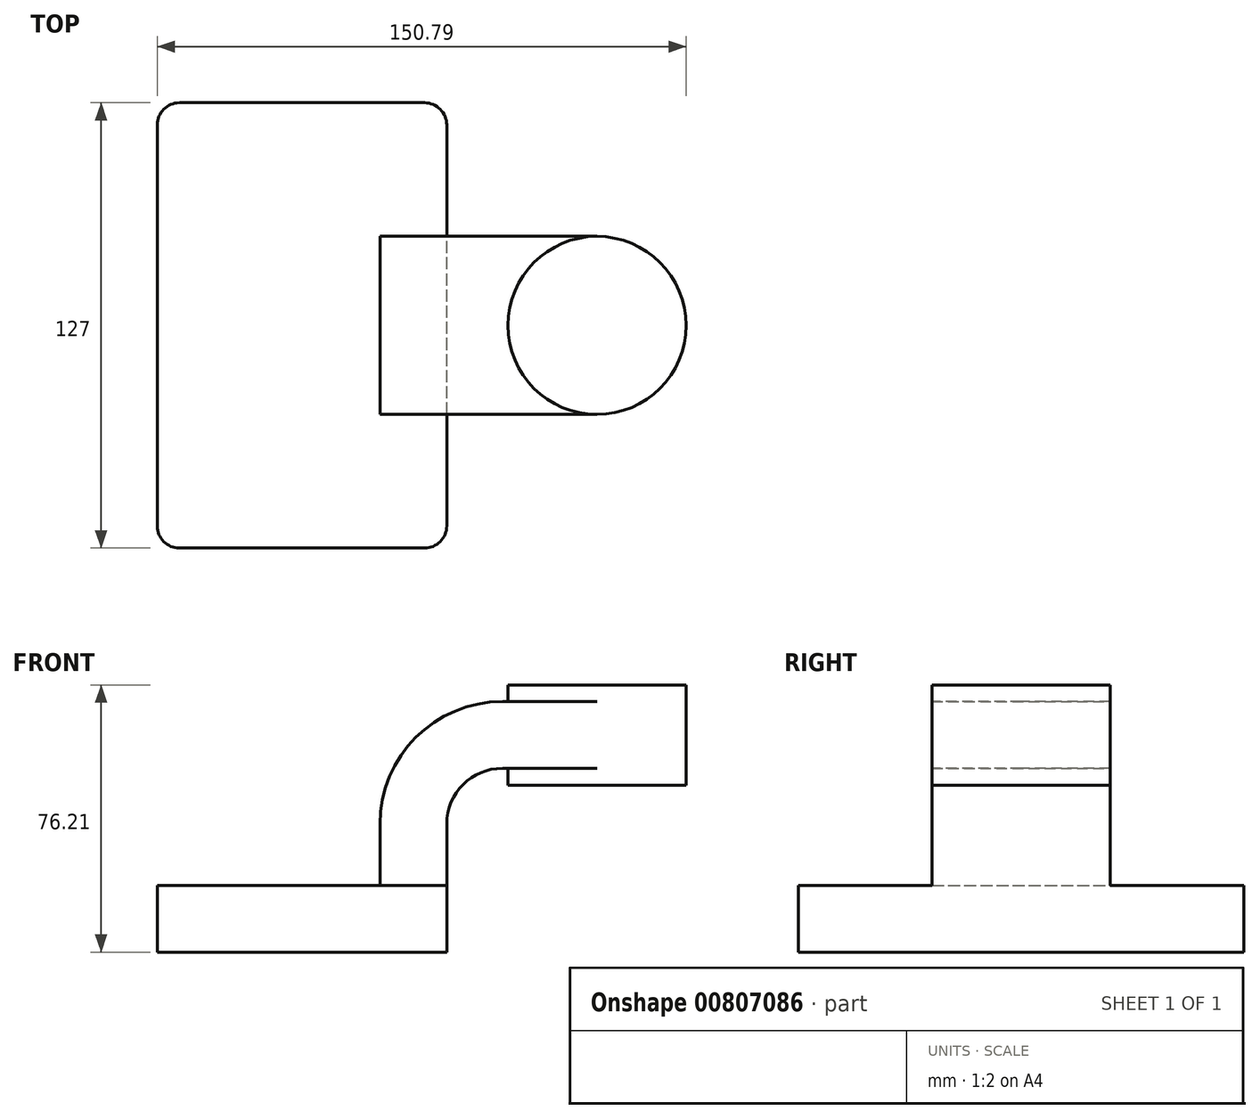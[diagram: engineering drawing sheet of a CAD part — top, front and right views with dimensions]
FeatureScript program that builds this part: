
annotation { "Feature Type Name" : "Feature", "Feature Type Description" : "" }
export const myFeature = defineFeature(function(context is Context, id is Id, definition is map)
    precondition{}
    {
        {
            var Q0;
            Q0=qCreatedBy(makeId("Front.planeOp"),FACE);
            var sketch = newSketch(context, id + "F0", { "sketchPlane" : qUnion([Q0])});
            skLineSegment(sketch, "E0.bottom", {"start": v(41.28, -9.52) * mm, "end": v(-41.27, -9.53) * mm});
            skLineSegment(sketch, "E0.top", {"start": v(41.27, 9.53) * mm, "end": v(-41.28, 9.53) * mm});
            skLineSegment(sketch, "E0.left", {"start": v(41.28, -9.52) * mm, "end": v(41.28, 9.53) * mm});
            skLineSegment(sketch, "E0.right", {"start": v(-41.27, -9.53) * mm, "end": v(-41.28, 9.53) * mm});
            skPoint(sketch, "E0.middle", {"position": v(0, 0) * mm});
            skLineSegment(sketch, "E1.bottom", {"start": v(109.52, 38.1) * mm, "end": v(58.72, 38.1) * mm});
            skLineSegment(sketch, "E1.top", {"start": v(109.52, 66.68) * mm, "end": v(58.72, 66.68) * mm});
            skLineSegment(sketch, "E1.left", {"start": v(109.52, 38.1) * mm, "end": v(109.52, 66.68) * mm});
            skLineSegment(sketch, "E1.right", {"start": v(58.72, 38.1) * mm, "end": v(58.72, 66.68) * mm});
            skPoint(sketch, "E1.middle", {"position": v(84.12, 52.39) * mm});
            skLineSegment(sketch, "E2", {"start": v(41.27, 9.53) * mm, "end": v(41.27, 27) * mm});
            skArc(sketch, "E3", {"start": v(41.27, 27) * mm, "mid": v(45.92, 38.23) * mm, "end": v(57.15, 42.88) * mm});
            skLineSegment(sketch, "E4", {"start": v(57.15, 42.88) * mm, "end": v(84.12, 42.88) * mm});
            skPoint(sketch, "E4.endSnap0", {"position": v(84.12, 38.1) * mm});
            skLineSegment(sketch, "E5.0", {"start": v(57.15, 61.93) * mm, "end": v(84.12, 61.93) * mm});
            skArc(sketch, "E5.1", {"start": v(22.23, 27) * mm, "mid": v(32.45, 51.7) * mm, "end": v(57.15, 61.93) * mm});
            skLineSegment(sketch, "E5.2", {"start": v(22.22, 9.53) * mm, "end": v(22.22, 27) * mm});
            skLineSegment(sketch, "E6", {"start": v(84.12, 42.88) * mm, "end": v(84.12, 61.93) * mm});
            skFitSpline(sketch, "E7", {"points": [v(-41.28, 9.52) * mm, v(57.15, 61.93) * mm], "startDerivative": vector(5.36, 73.67) * mm, "endDerivative": vector(130.36, -0.71) * mm});
            skLineSegment(sketch, "E8", {"start": v(84.12, 38.1) * mm, "end": v(84.12, 66.68) * mm});
            skSolve(sketch);
        }
        {
            var Q0;
            Q0=makeQuery(id+"F0.imprint","IMPRINT",FACE,{"disambiguationData":[TD([[makeQuery(id+"F0.imprint","IMPRINT",EDGE,{"derivedFrom":sQuery(id+"F0.wireOp",EDGE,"E0.bottom")}),-1.0]])]});
            extrude(context, id + "F1", {"entities" : qUnion([Q0]), "endBound" : BoundingType.SYMMETRIC, "depth" : 127 * mm, "offsetDistance" : 25.4 * mm});
        }
        {
            var Q0;
            {var subQ1=sQuery(id+"F0.wireOp",EDGE,"E2");Q0=makeQuery(id+"F0.imprint","IMPRINT",FACE,{"disambiguationData":[TD([[makeQuery(id+"F0.imprint","IMPRINT",EDGE,{"derivedFrom":subQ1}),1.0]])]});}
            var Q1;
            {var subQ5=sQuery(id+"F0.wireOp",EDGE,"E6");Q1=makeQuery(id+"F0.imprint","IMPRINT",FACE,{"disambiguationData":[TD([[makeQuery(id+"F0.imprint","IMPRINT",EDGE,{"derivedFrom":subQ5}),1.0]])]});}
            var Q2;
            {var subQ0=sQuery(id+"F0.wireOp",EDGE,"E4");var subQ1=sQuery(id+"F0.wireOp",EDGE,"E1.right");var subQ2=makeQuery(id+"F0.imprint","INTERSECT",VERTEX,{"derivedFrom":[subQ1,subQ0]});Q2=makeQuery(id+"F0.imprint","IMPRINT",FACE,{"disambiguationData":[TD([[makeQuery(id+"F0.imprint","IMPRINT",EDGE,{"disambiguationData":[TD([[subQ2,-1.0]])],"derivedFrom":subQ1}),-1.0]])]});}
            extrude(context, id + "F2", {"entities" : qUnion([Q0, Q1, Q2]), "operationType" : NewBodyOperationType.ADD, "endBound" : BoundingType.SYMMETRIC, "depth" : 50.8 * mm, "offsetDistance" : 25.4 * mm});
        }
        {
            var Q0;
            Q0=makeQuery(id+"F0.imprint","IMPRINT",FACE,{"disambiguationData":[TD([[makeQuery(id+"F0.imprint","IMPRINT",EDGE,{"derivedFrom":sQuery(id+"F0.wireOp",EDGE,"E5.1")}),1.0]])]});
            extrude(context, id + "F3", {"entities" : qUnion([Q0]), "operationType" : NewBodyOperationType.ADD, "endBound" : BoundingType.SYMMETRIC, "depth" : 15.88 * mm, "offsetDistance" : 25.4 * mm});
        }
        {
            var Q0;
            {var subQ0=sQuery(id+"F0.wireOp",EDGE,"E1.left");Q0=makeQuery(id+"F0.imprint","IMPRINT",FACE,{"disambiguationData":[TD([[makeQuery(id+"F0.imprint","IMPRINT",EDGE,{"derivedFrom":subQ0}),1.0]])]});}
            var Q1;
            Q1=sQuery(id+"F0.wireOp",EDGE,"E8");
            revolve(context, id + "F4", {"operationType" : NewBodyOperationType.ADD, "surfaceOperationType" : NewSurfaceOperationType.NEW, "entities" : qUnion([Q0]), "axis" : qUnion([Q1]), "revolveType" : RevolveType.FULL});
        }
        {
            var Q0;
            Q0=makeQuery(id+"F1.opExtrude","CAP_EDGE",EDGE,{"disambiguationData":[OSD([sQuery(id+"F0.wireOp",EDGE,"E0.left")])],"isStart":false});
            var Q1;
            Q1=makeQuery(id+"F1.opExtrude","CAP_EDGE",EDGE,{"disambiguationData":[OSD([sQuery(id+"F0.wireOp",EDGE,"E0.right")])],"isStart":false});
            var Q2;
            Q2=makeQuery(id+"F1.opExtrude","CAP_EDGE",EDGE,{"disambiguationData":[OSD([sQuery(id+"F0.wireOp",EDGE,"E0.left")])],"isStart":true});
            var Q3;
            Q3=makeQuery(id+"F1.opExtrude","CAP_EDGE",EDGE,{"disambiguationData":[OSD([sQuery(id+"F0.wireOp",EDGE,"E0.right")])],"isStart":true});
            fillet(context, id + "F5", {"entities" : qUnion([Q0, Q1, Q2, Q3]), "radius" : 6.35 * mm, "tangentPropagation" : true, "allowEdgeOverflow" : false});
        }
    });
